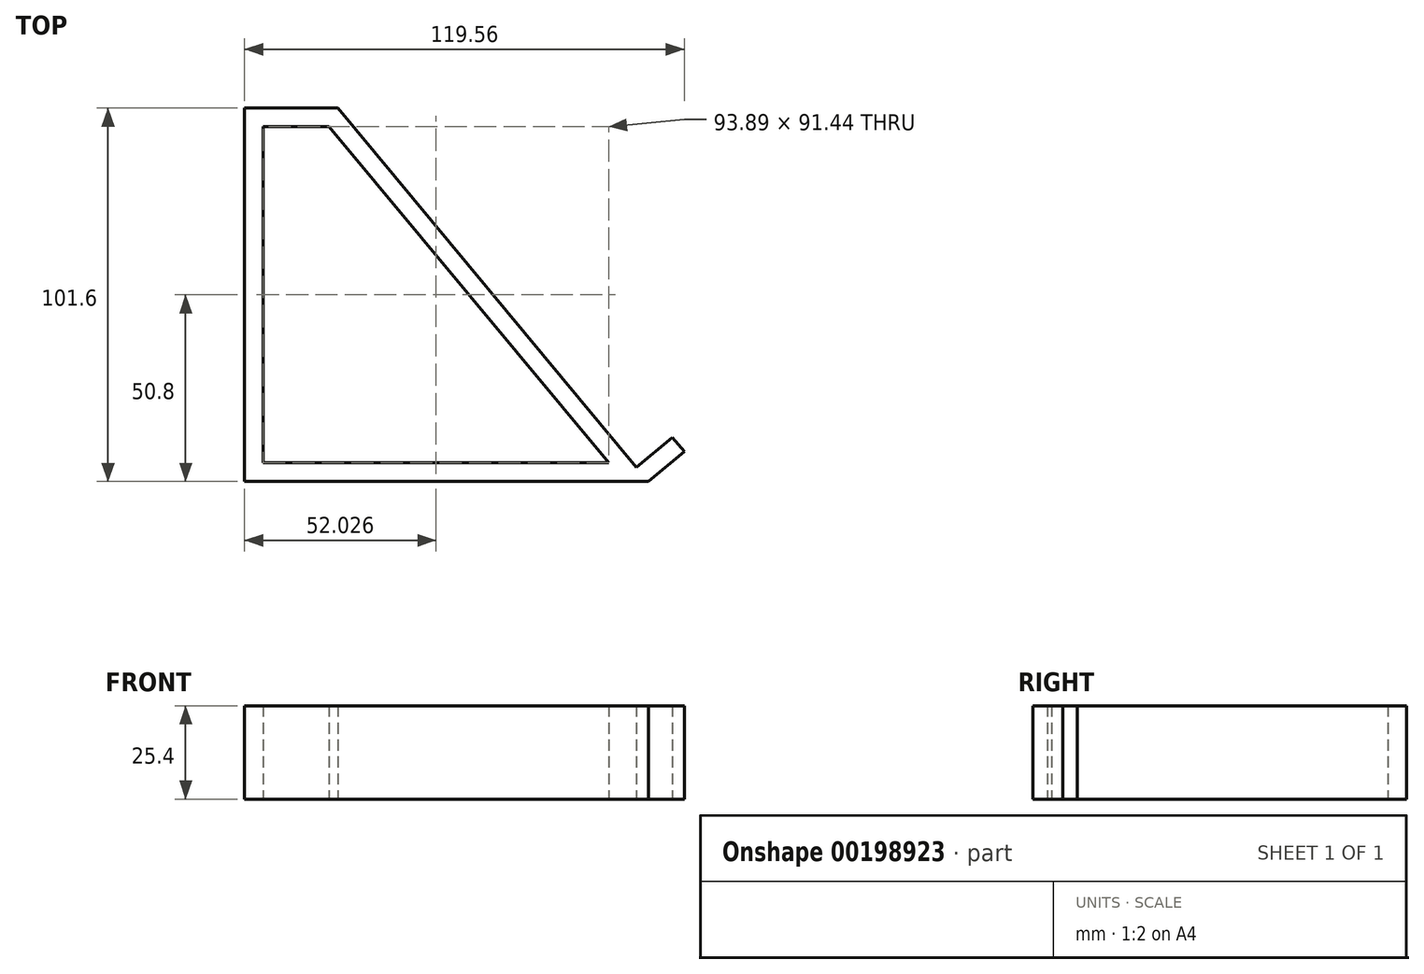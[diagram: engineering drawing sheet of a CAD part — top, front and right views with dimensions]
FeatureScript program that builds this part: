
annotation { "Feature Type Name" : "Feature", "Feature Type Description" : "" }
export const myFeature = defineFeature(function(context is Context, id is Id, definition is map)
    precondition{}
    {
        {
            var Q0;
            Q0=qCreatedBy(makeId("Top.planeOp"),FACE);
            var sketch = newSketch(context, id + "F0", { "sketchPlane" : qUnion([Q0])});
            skLineSegment(sketch, "E0", {"start": v(0, 0) * mm, "end": v(84.4, 0) * mm});
            skLineSegment(sketch, "E1", {"start": v(0, 0) * mm, "end": v(0, 101.6) * mm, "construction": true});
            skLineSegment(sketch, "E2", {"start": v(0, 101.6) * mm, "end": v(81.15, 3.9) * mm});
            skLineSegment(sketch, "E3", {"start": v(84.4, 0) * mm, "end": v(94.16, 8.11) * mm});
            skLineSegment(sketch, "E4", {"start": v(0, 101.6) * mm, "end": v(-25.4, 101.6) * mm});
            skLineSegment(sketch, "E5", {"start": v(-25.4, 101.6) * mm, "end": v(-25.4, 0) * mm});
            skLineSegment(sketch, "E6", {"start": v(-25.4, 0) * mm, "end": v(0, 0) * mm});
            skLineSegment(sketch, "E7.0", {"start": v(-2.38, 96.52) * mm, "end": v(73.57, 5.08) * mm});
            skPoint(sketch, "E8", {"position": v(77.8, 0) * mm});
            skLineSegment(sketch, "E9.0", {"start": v(-2.38, 96.52) * mm, "end": v(-20.32, 96.52) * mm});
            skLineSegment(sketch, "E10.0", {"start": v(-20.32, 96.52) * mm, "end": v(-20.32, 5.08) * mm});
            skLineSegment(sketch, "E11.0", {"start": v(0, 5.08) * mm, "end": v(73.57, 5.08) * mm});
            skLineSegment(sketch, "E11.1", {"start": v(-20.32, 5.08) * mm, "end": v(0, 5.08) * mm});
            skLineSegment(sketch, "E12.0", {"start": v(81.15, 3.9) * mm, "end": v(90.92, 12.02) * mm});
            skLineSegment(sketch, "E13", {"start": v(90.92, 12.02) * mm, "end": v(94.16, 8.11) * mm});
            skSolve(sketch);
        }
        {
            var Q0;
            Q0=makeQuery(id+"F0.imprint","IMPRINT",FACE,{"disambiguationData":[TD([[makeQuery(id+"F0.imprint","IMPRINT",EDGE,{"derivedFrom":sQuery(id+"F0.wireOp",EDGE,"E0")}),1.0]])]});
            extrude(context, id + "F1", {"entities" : qUnion([Q0]), "depth" : 25.4 * mm});
        }
    });
